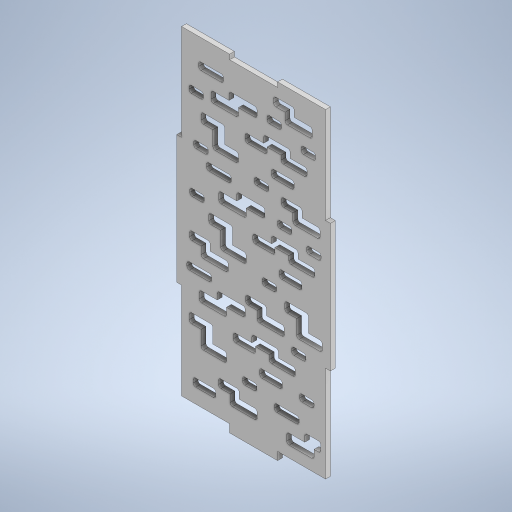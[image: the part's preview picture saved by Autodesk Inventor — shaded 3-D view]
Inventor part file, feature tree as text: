
AUTODESK INVENTOR PART (.ipt)
format: ipt  version: 2023 (Build 270158000, 158)  size: 807,424 bytes
history: native  units: mm
features: extrude x2, sketch x1
ambient origin geometry x8: Origin, YZ Plane, XZ Plane, XY Plane, X Axis, Y Axis, Z Axis, Center Point
bodies: Solide1 (feature_tree)
feature tree (3):
  extrude  "Extrusion1"  Depth=33.0mm
  extrude  "Extrusion2"  Depth=33.0mm
  sketch  "Esquisse1"
